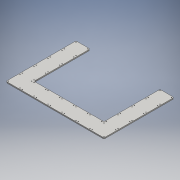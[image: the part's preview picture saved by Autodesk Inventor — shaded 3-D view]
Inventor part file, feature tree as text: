
AUTODESK INVENTOR PART (.ipt)
format: ipt  version: 2016 (Build 200138000, 138)  size: 301,568 bytes
history: native  units: mm
features: extrude x1, fillet x1
ambient origin geometry x8: Origin, YZ Plane, XZ Plane, XY Plane, X Axis, Y Axis, Z Axis, Center Point
bodies: Body1 (feature_tree)
feature tree (2):
  extrude  "Frame"  Depth=420.0mm
  fillet  "Fillet1"  Radius=300.0mm
